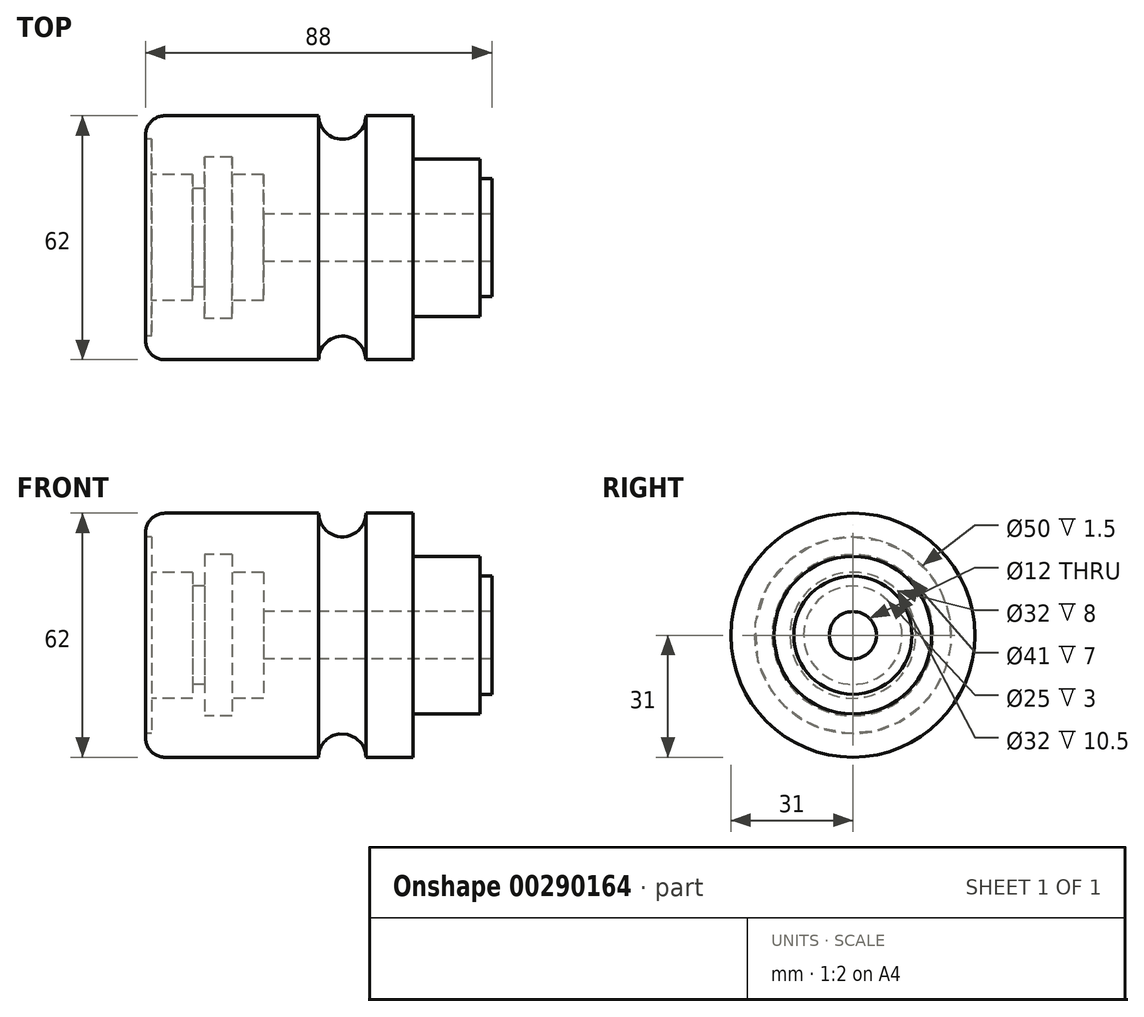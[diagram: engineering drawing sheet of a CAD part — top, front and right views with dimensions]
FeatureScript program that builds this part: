
annotation { "Feature Type Name" : "Feature", "Feature Type Description" : "" }
export const myFeature = defineFeature(function(context is Context, id is Id, definition is map)
    precondition{}
    {
        {
            var Q0;
            Q0=qCreatedBy(makeId("Front.planeOp"),FACE);
            var sketch = newSketch(context, id + "F0", { "sketchPlane" : qUnion([Q0])});
            skLineSegment(sketch, "E0", {"start": v(0, 0) * mm, "end": v(127.48, 0) * mm, "construction": true});
            skLineSegment(sketch, "E1", {"start": v(0, 0) * mm, "end": v(0, 31) * mm});
            skLineSegment(sketch, "E2", {"start": v(0, 31) * mm, "end": v(44, 31) * mm});
            skLineSegment(sketch, "E3", {"start": v(68, 31) * mm, "end": v(68, 20) * mm});
            skLineSegment(sketch, "E4", {"start": v(68, 20) * mm, "end": v(85, 20) * mm});
            skLineSegment(sketch, "E5", {"start": v(85, 20) * mm, "end": v(85, 15) * mm});
            skLineSegment(sketch, "E6", {"start": v(85, 15) * mm, "end": v(88, 15) * mm});
            skLineSegment(sketch, "E7", {"start": v(88, 15) * mm, "end": v(88, 0) * mm});
            skArc(sketch, "E8", {"start": v(44, 31) * mm, "mid": v(50, 25) * mm, "end": v(56, 31) * mm});
            skLineSegment(sketch, "E9.trimOffspring", {"start": v(56, 31) * mm, "end": v(68, 31) * mm});
            skLineSegment(sketch, "E10", {"start": v(88, 0) * mm, "end": v(0, 0) * mm});
            skSolve(sketch);
        }
        {
            var Q0;
            Q0=qCreatedBy(makeId("Front.planeOp"),FACE);
            var sketch = newSketch(context, id + "F1", { "sketchPlane" : qUnion([Q0])});
            skLineSegment(sketch, "E11", {"start": v(0, 25) * mm, "end": v(1.5, 25) * mm});
            skLineSegment(sketch, "E12", {"start": v(1.5, 25) * mm, "end": v(1.5, 16) * mm});
            skLineSegment(sketch, "E13", {"start": v(1.5, 16) * mm, "end": v(12, 16) * mm});
            skLineSegment(sketch, "E14", {"start": v(12, 16) * mm, "end": v(12, 12.5) * mm});
            skLineSegment(sketch, "E15", {"start": v(12, 12.5) * mm, "end": v(15, 12.5) * mm});
            skLineSegment(sketch, "E16", {"start": v(88, 6) * mm, "end": v(88, 0) * mm});
            skLineSegment(sketch, "E17", {"start": v(88, 0) * mm, "end": v(0, 0) * mm});
            skLineSegment(sketch, "E18", {"start": v(0, 0) * mm, "end": v(-29.86, 0) * mm, "construction": true});
            skLineSegment(sketch, "E19", {"start": v(15, 12.5) * mm, "end": v(15, 20.5) * mm});
            skLineSegment(sketch, "E20", {"start": v(15, 20.5) * mm, "end": v(22, 20.5) * mm});
            skLineSegment(sketch, "E21", {"start": v(22, 20.5) * mm, "end": v(22, 16) * mm});
            skLineSegment(sketch, "E22", {"start": v(22, 16) * mm, "end": v(30, 16) * mm});
            skLineSegment(sketch, "E23", {"start": v(30, 16) * mm, "end": v(30, 6) * mm});
            skLineSegment(sketch, "E24", {"start": v(30, 6) * mm, "end": v(88, 6) * mm});
            skLineSegment(sketch, "E25", {"start": v(0, 0) * mm, "end": v(0, 25) * mm});
            skSolve(sketch);
        }
        {
            var Q0;
            Q0 = qSketchRegion(id + "F0", true);
            var Q1;
            Q1=sQuery(id+"F0.wireOp",EDGE,"E0");
            revolve(context, id + "F2", {"entities" : qUnion([Q0]), "axis" : qUnion([Q1]), "revolveType" : RevolveType.FULL});
        }
        {
            var Q0;
            Q0 = qSketchRegion(id + "F1", true);
            var Q1;
            Q1=sQuery(id+"F1.wireOp",EDGE,"E18");
            revolve(context, id + "F3", {"operationType" : NewBodyOperationType.REMOVE, "entities" : qUnion([Q0]), "axis" : qUnion([Q1]), "revolveType" : RevolveType.FULL, "oppositeDirection" : true});
        }
        {
            var Q0;
            Q0=makeQuery(id+"F2.opRevolve","SWEPT_EDGE",EDGE,{"disambiguationData":[OSD([sQuery(id+"F0.wireOp",EDGE,"E1"),sQuery(id+"F0.wireOp",EDGE,"E2")])]});
            fillet(context, id + "F4", {"entities" : qUnion([Q0]), "radius" : 5 * mm, "tangentPropagation" : true, "allowEdgeOverflow" : false});
        }
    });
